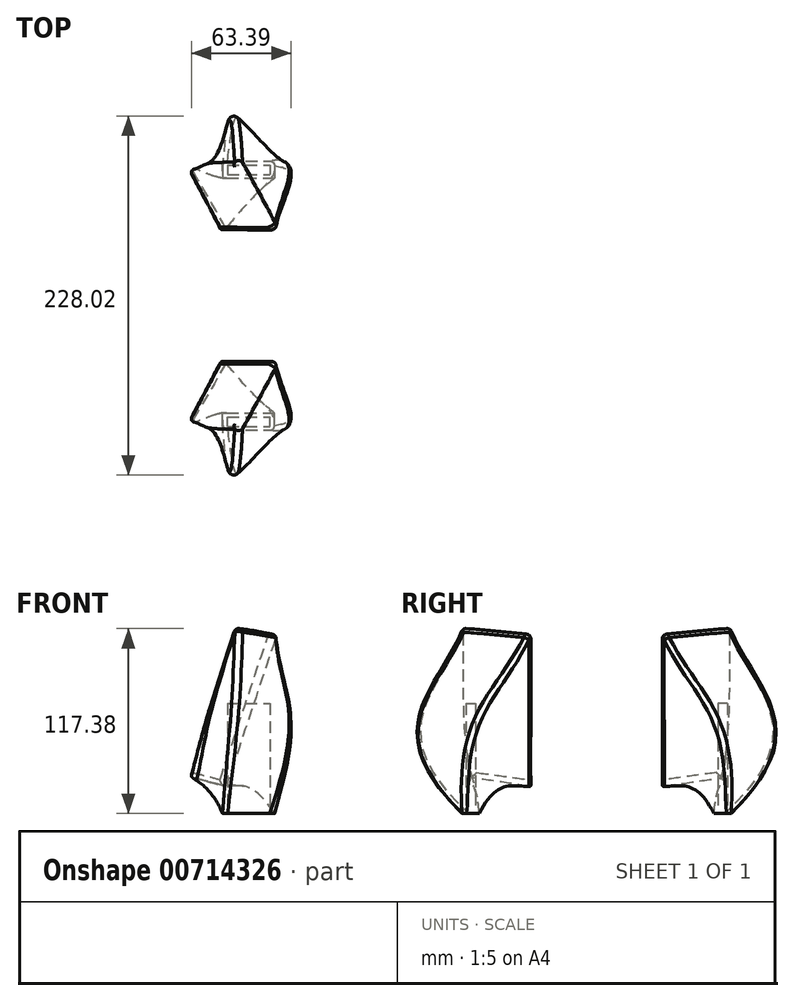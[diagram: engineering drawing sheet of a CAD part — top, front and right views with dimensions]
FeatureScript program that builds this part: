
annotation { "Feature Type Name" : "Feature", "Feature Type Description" : "" }
export const myFeature = defineFeature(function(context is Context, id is Id, definition is map)
    precondition{}
    {
        {
            var Q0;
            Q0=qCreatedBy(makeId("Top.planeOp"),FACE);
            var sketch = newSketch(context, id + "F0", { "sketchPlane" : qUnion([Q0])});
            skLineSegment(sketch, "E0.bottom", {"start": v(-16.5, 5.5) * mm, "end": v(16.5, 5.5) * mm});
            skLineSegment(sketch, "E0.top", {"start": v(-16.5, -5.5) * mm, "end": v(16.5, -5.5) * mm});
            skLineSegment(sketch, "E0.left", {"start": v(-16.5, 5.5) * mm, "end": v(-16.5, -5.5) * mm});
            skLineSegment(sketch, "E0.right", {"start": v(16.5, 5.5) * mm, "end": v(16.5, -5.5) * mm});
            skSolve(sketch);
        }
        {
            var Q0;
            Q0=qCreatedBy(makeId("Top.planeOp"),FACE);
            cPlane(context, id + "F1", {"entities" : qUnion([Q0]), "cplaneType" : CPlaneType.OFFSET, "offset" : 80 * mm, "width" : 150 * mm, "height" : 150 * mm});
        }
        {
            var Q0;
            Q0=qCreatedBy(id+"F1.planeOp",FACE);
            var sketch = newSketch(context, id + "F2", { "sketchPlane" : qUnion([Q0])});
            skLineSegment(sketch, "E1", {"start": v(16.5, -5.5) * mm, "end": v(-16.5, -5.5) * mm});
            skLineSegment(sketch, "E2", {"start": v(-16.5, -5.5) * mm, "end": v(8.1, -48.13) * mm});
            skSolve(sketch);
        }
        {
            var Q0;
            Q0=qCreatedBy(makeId("Right.planeOp"),FACE);
            var Q1;
            Q1=sQuery(id+"F2.wireOp",VERTEX,"E2.start");
            cPlane(context, id + "F3", {"entities" : qUnion([Q0, Q1]), "cplaneType" : CPlaneType.PLANE_POINT, "offset" : 25 * mm, "oppositeDirection" : true, "width" : 150 * mm, "height" : 150 * mm});
        }
        {
            var Q0;
            Q0=qCreatedBy(id+"F3.planeOp",FACE);
            var sketch = newSketch(context, id + "F4", { "sketchPlane" : qUnion([Q0])});
            skLineSegment(sketch, "E3", {"start": v(-5.5, 35.4) * mm, "end": v(-5.5, 80) * mm});
            skLineSegment(sketch, "E4", {"start": v(-5.5, 80) * mm, "end": v(-21.68, 51.97) * mm});
            skSolve(sketch);
        }
        {
            var Q0;
            Q0=sQuery(id+"F2.wireOp",VERTEX,"E2.end");
            var Q1;
            Q1=sQuery(id+"F4.wireOp",VERTEX,"E4.end");
            var Q2;
            Q2=sQuery(id+"F4.wireOp",VERTEX,"E4.start");
            cPlane(context, id + "F5", {"entities" : qUnion([Q0, Q1, Q2]), "cplaneType" : CPlaneType.THREE_POINT, "offset" : 25 * mm, "width" : 150 * mm, "height" : 150 * mm});
        }
        {
            var Q0;
            Q0=qCreatedBy(id+"F5.planeOp",FACE);
            var sketch = newSketch(context, id + "F6", { "sketchPlane" : qUnion([Q0])});
            skLineSegment(sketch, "E5.bottom", {"start": v(-24.85, 120.68) * mm, "end": v(25.15, 120.68) * mm});
            skLineSegment(sketch, "E5.top", {"start": v(-24.85, 10.68) * mm, "end": v(25.15, 10.68) * mm});
            skLineSegment(sketch, "E5.left", {"start": v(-24.85, 120.68) * mm, "end": v(-24.85, 10.68) * mm});
            skLineSegment(sketch, "E5.right", {"start": v(25.15, 120.68) * mm, "end": v(25.15, 10.68) * mm});
            skSolve(sketch);
        }
        {
            var Q0;
            Q0=sQuery(id+"F0.wireOp",VERTEX,"E0.right.end");
            var Q1;
            Q1=sQuery(id+"F6.wireOp",VERTEX,"E5.right.end");
            var Q2;
            Q2=sQuery(id+"F6.wireOp",VERTEX,"E5.left.start");
            cPlane(context, id + "F7", {"entities" : qUnion([Q0, Q1, Q2]), "cplaneType" : CPlaneType.THREE_POINT, "offset" : 25 * mm, "width" : 150 * mm, "height" : 150 * mm});
        }
        {
            var Q0;
            Q0=sQuery(id+"F6.wireOp",VERTEX,"E5.left.end");
            var Q1;
            Q1=sQuery(id+"F0.wireOp",VERTEX,"E0.left.end");
            var Q2;
            Q2=sQuery(id+"F6.wireOp",VERTEX,"E5.right.start");
            cPlane(context, id + "F8", {"entities" : qUnion([Q0, Q1, Q2]), "cplaneType" : CPlaneType.THREE_POINT, "offset" : 25 * mm, "width" : 150 * mm, "height" : 150 * mm});
        }
        {
            var Q0;
            Q0=sQuery(id+"F0.wireOp",VERTEX,"E0.bottom.start");
            var Q1;
            Q1=sQuery(id+"F6.wireOp",VERTEX,"E5.left.start");
            var Q2;
            Q2=sQuery(id+"F6.wireOp",VERTEX,"E5.right.end");
            cPlane(context, id + "F9", {"entities" : qUnion([Q0, Q1, Q2]), "cplaneType" : CPlaneType.THREE_POINT, "offset" : 25 * mm, "width" : 150 * mm, "height" : 150 * mm});
        }
        {
            var Q0;
            Q0=sQuery(id+"F6.wireOp",VERTEX,"E5.right.start");
            var Q1;
            Q1=sQuery(id+"F0.wireOp",VERTEX,"E0.right.start");
            var Q2;
            Q2=sQuery(id+"F6.wireOp",VERTEX,"E5.right.end");
            cPlane(context, id + "F10", {"entities" : qUnion([Q0, Q1, Q2]), "cplaneType" : CPlaneType.THREE_POINT, "offset" : 25 * mm, "width" : 150 * mm, "height" : 150 * mm});
        }
        {
            var Q0;
            Q0=qCreatedBy(id+"F7.planeOp",FACE);
            var sketch = newSketch(context, id + "F11", { "sketchPlane" : qUnion([Q0])});
            skFitSpline(sketch, "E6", {"points": [v(6.05, -3.65) * mm, v(-39.56, 20.4) * mm], "startDerivative": vector(-45.43, 76.02) * mm, "endDerivative": vector(-56.53, 8.3) * mm});
            skSolve(sketch);
        }
        {
            var Q0;
            Q0=qCreatedBy(id+"F8.planeOp",FACE);
            var sketch = newSketch(context, id + "F12", { "sketchPlane" : qUnion([Q0])});
            skFitSpline(sketch, "E7", {"points": [v(12.16, 0.78) * mm, v(38.65, 23.89) * mm], "startDerivative": vector(19.08, 37.76) * mm, "endDerivative": vector(37.48, 12.3) * mm});
            skSolve(sketch);
        }
        {
            var Q0;
            Q0=qCreatedBy(id+"F9.planeOp",FACE);
            var sketch = newSketch(context, id + "F13", { "sketchPlane" : qUnion([Q0])});
            skFitSpline(sketch, "E8", {"points": [v(-4.7, -1.45) * mm, v(-2.47, 128) * mm], "startDerivative": vector(-183.14, 176.37) * mm, "endDerivative": vector(43.56, 140.8) * mm});
            skSolve(sketch);
        }
        {
            var Q0;
            Q0=qCreatedBy(id+"F10.planeOp",FACE);
            var sketch = newSketch(context, id + "F14", { "sketchPlane" : qUnion([Q0])});
            skFitSpline(sketch, "E9", {"points": [v(14.13, 5.22) * mm, v(-45.2, 120.68) * mm], "startDerivative": vector(7.34, 225.07) * mm, "endDerivative": vector(-79.07, 133.25) * mm});
            skSolve(sketch);
        }
        {
            var Q0;
            Q0=makeQuery(id+"F0.imprint","IMPRINT",FACE,{"disambiguationData":[TD([[makeQuery(id+"F0.imprint","IMPRINT",EDGE,{"derivedFrom":sQuery(id+"F0.wireOp",EDGE,"E0.bottom")}),-1.0]])]});
            var Q1;
            Q1=makeQuery(id+"F6.imprint","IMPRINT",FACE,{"disambiguationData":[TD([[makeQuery(id+"F6.imprint","IMPRINT",EDGE,{"derivedFrom":sQuery(id+"F6.wireOp",EDGE,"E5.bottom")}),-1.0]])]});
            var Q2;
            Q2=sQuery(id+"F11.wireOp",EDGE,"E6");
            var Q3;
            Q3=sQuery(id+"F12.wireOp",EDGE,"E7");
            var Q4;
            Q4=sQuery(id+"F13.wireOp",EDGE,"E8");
            var Q5;
            Q5=sQuery(id+"F14.wireOp",EDGE,"E9");
            loft(context, id + "F15", {"addGuides" : true, "sheetProfilesArray" : [{ "sheetProfileEntities" : qUnion([Q0]) }, { "sheetProfileEntities" : qUnion([Q1]) }], "guidesArray" : [{ "guideEntities" : qUnion([Q2]), "guideDerivativeType" : LoftGuideDerivativeType.DEFAULT, "guideDerivativeMagnitude" : 1 }, { "guideEntities" : qUnion([Q3]), "guideDerivativeType" : LoftGuideDerivativeType.DEFAULT, "guideDerivativeMagnitude" : 1 }, { "guideEntities" : qUnion([Q4]), "guideDerivativeType" : LoftGuideDerivativeType.DEFAULT, "guideDerivativeMagnitude" : 1 }, { "guideEntities" : qUnion([Q5]), "guideDerivativeType" : LoftGuideDerivativeType.DEFAULT, "guideDerivativeMagnitude" : 1 }]});
        }
        {
            var Q0;
            Q0=makeQuery(id+"F0.imprint","IMPRINT",FACE,{"disambiguationData":[TD([[makeQuery(id+"F0.imprint","IMPRINT",EDGE,{"derivedFrom":sQuery(id+"F0.wireOp",EDGE,"E0.bottom")}),-1.0]])]});
            var sketch = newSketch(context, id + "F16", { "sketchPlane" : qUnion([Q0])});
            skLineSegment(sketch, "E10.bottom", {"start": v(-13.5, 3) * mm, "end": v(13.5, 3) * mm});
            skLineSegment(sketch, "E10.top", {"start": v(-13.5, -3) * mm, "end": v(13.5, -3) * mm});
            skLineSegment(sketch, "E10.left", {"start": v(-13.5, 3) * mm, "end": v(-13.5, -3) * mm});
            skLineSegment(sketch, "E10.right", {"start": v(13.5, 3) * mm, "end": v(13.5, -3) * mm});
            skLineSegment(sketch, "E11", {"start": v(24.36, 0) * mm, "end": v(-23.78, 0) * mm, "construction": true});
            skPoint(sketch, "E11.startSnap0", {"position": v(-13.5, 0) * mm});
            skLineSegment(sketch, "E12", {"start": v(0, -9.59) * mm, "end": v(0, 11.77) * mm, "construction": true});
            skSolve(sketch);
        }
        {
            var Q0;
            Q0=makeQuery(id+"F16.imprint","IMPRINT",FACE,{"disambiguationData":[TD([[makeQuery(id+"F16.imprint","IMPRINT",EDGE,{"derivedFrom":sQuery(id+"F16.wireOp",EDGE,"E10.bottom")}),-1.0]])]});
            extrude(context, id + "F17", {"entities" : qUnion([Q0]), "operationType" : NewBodyOperationType.REMOVE, "depth" : 70 * mm, "offsetDistance" : 25 * mm});
        }
        {
            var Q0;
            Q0=makeQuery(id+"F15.opLoft","CAP_FACE",FACE,{"disambiguationData":[OSD([makeQuery(id+"F6.imprint","IMPRINT",FACE,{"disambiguationData":[TD([[makeQuery(id+"F6.imprint","IMPRINT",EDGE,{"derivedFrom":sQuery(id+"F6.wireOp",EDGE,"E5.bottom")}),-1.0]])]})])],"isStart":true});
            var Q1;
            Q1=makeQuery(id+"F15.opLoft","SWEPT_EDGE",EDGE,{"disambiguationData":[OSD([sQuery(id+"F0.wireOp",EDGE,"E0.bottom"),sQuery(id+"F0.wireOp",EDGE,"E0.left"),sQuery(id+"F6.wireOp",EDGE,"E5.bottom"),sQuery(id+"F6.wireOp",EDGE,"E5.left")])]});
            var Q2;
            Q2=makeQuery(id+"F15.opLoft","SWEPT_EDGE",EDGE,{"disambiguationData":[OSD([sQuery(id+"F13.wireOp",EDGE,"E8")])]});
            var Q3;
            Q3=makeQuery(id+"F15.opLoft","SWEPT_EDGE",EDGE,{"disambiguationData":[OSD([sQuery(id+"F14.wireOp",EDGE,"E9")])]});
            fillet(context, id + "F18", {"entities" : qUnion([Q0, Q1, Q2, Q3]), "radius" : 3 * mm, "tangentPropagation" : true, "allowEdgeOverflow" : false});
        }
        {
            var Q0;
            Q0=qCreatedBy(makeId("Front.planeOp"),FACE);
            cPlane(context, id + "F19", {"entities" : qUnion([Q0]), "cplaneType" : CPlaneType.OFFSET, "offset" : 80 * mm, "width" : 150 * mm, "height" : 150 * mm});
        }
        {
            var Q0;
            Q0=makeQuery(id+"F15.opLoft","SWEPT_BODY",BODY,{"disambiguationData":[OSD([makeQuery(id+"F0.imprint","IMPRINT",FACE,{"disambiguationData":[TD([[makeQuery(id+"F0.imprint","IMPRINT",EDGE,{"derivedFrom":sQuery(id+"F0.wireOp",EDGE,"E0.bottom")}),-1.0]])]}),makeQuery(id+"F6.imprint","IMPRINT",FACE,{"disambiguationData":[TD([[makeQuery(id+"F6.imprint","IMPRINT",EDGE,{"derivedFrom":sQuery(id+"F6.wireOp",EDGE,"E5.bottom")}),-1.0]])]}),sQuery(id+"F11.wireOp",EDGE,"E6"),sQuery(id+"F12.wireOp",EDGE,"E7")])]});
            var Q1;
            Q1=qCreatedBy(id+"F19.planeOp",FACE);
            mirror(context, id + "F20", {"entities" : qUnion([Q0]), "mirrorPlane" : qUnion([Q1])});
        }
    });
